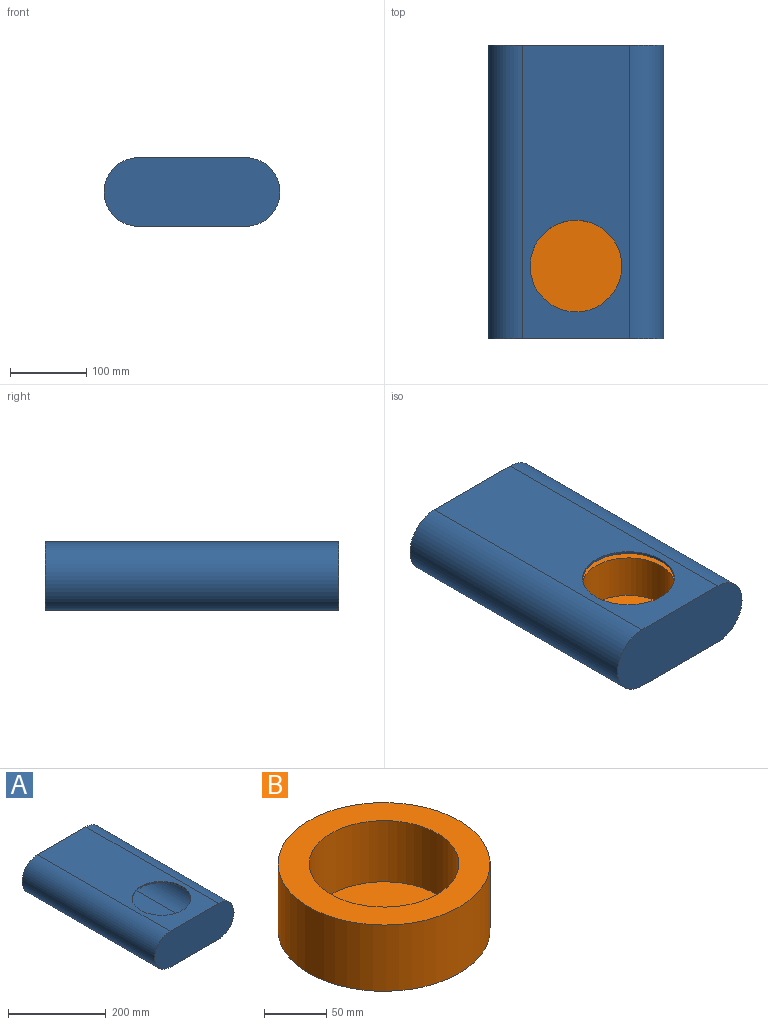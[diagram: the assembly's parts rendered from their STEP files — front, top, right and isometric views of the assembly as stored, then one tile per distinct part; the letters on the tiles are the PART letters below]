
ASSEMBLY  parts=2 mates=1
PART A: 13 faces, bbox 230x384x90 mm
  f0: plane 230x90mm, normal (0,1,0), area 1660mm2, adj f2,f3,f4,f5,f7,f8,f9,f10
  f1: plane 230x90mm, normal (0,-1,0), area 18961.7mm2, adj f2,f3,f4,f5
  f2: plane 384x140mm, normal (0,0,1), area 42450.3mm2, adj f0,f1,f4,f5,f11
  f3: plane 384x140mm, normal (0,0,-1), area 48733.5mm2, adj f0,f1,f4,f5,f12
  f4: cylinder r=45mm len=384mm, axis (0,-1,0), area 54286.7mm2, adj f0,f1,f2,f3
  f5: cylinder r=45mm len=384mm, axis (0,1,0), area 54286.7mm2, adj f0,f1,f2,f3
  f6: plane 224x84mm, normal (0,1,0), area 17301.8mm2, adj f7,f8,f9,f10
  f7: plane 381x140mm, normal (0,0,-1), area 42030.3mm2, adj f0,f6,f9,f10,f11
  f8: plane 381x140mm, normal (0,0,1), area 48313.5mm2, adj f0,f6,f9,f10,f12
  f9: cylinder r=42mm len=381mm, axis (0,-1,0), area 50271.8mm2, adj f0,f6,f7,f8
  f10: cylinder r=42mm len=381mm, axis (0,1,0), area 50271.8mm2, adj f0,f6,f7,f8
  f11: cylinder r=60mm len=120mm, axis (0,0,1), area 1131mm2, adj f2,f7
  f12: cylinder r=40mm len=80mm, axis (0,0,1), area 754mm2, adj f3,f8
PART B: 8 faces, bbox 170x170x80 mm
  f0: cylinder r=60mm len=120mm, axis (0,0,-1), area 22619.5mm2, adj f2,f4
  f1: cylinder r=85mm len=170mm, axis (0,0,-1), area 34714.6mm2, adj f2,f3
  f2: plane 170x170mm, normal (0,0,1), area 11388.3mm2, adj f0,f1
  f3: plane 170x170mm, normal (0,0,-1), area 17671.5mm2, adj f1,f5
  f4: plane 120x120mm, normal (0,0,1), area 11309.7mm2, adj f0
  f5: cylinder r=40mm len=80mm, axis (0,0,-1), area 2513.3mm2, adj f3,f7
  f6: plane 70x70mm, normal (0,0,-1), area 3848.5mm2, adj f7
  f7: torus R=35mm, axis (0,0,1), area 1884.3mm2, adj f5,f6
PLACE A t=(14.21,-147.54,132.68)mm
PLACE B t=(14.21,-147.54,147.68)mm
MATE fastened B.f5 <-> A.f11  axis (0,0,-1) through (14.21,-147.54,132.68)mm
